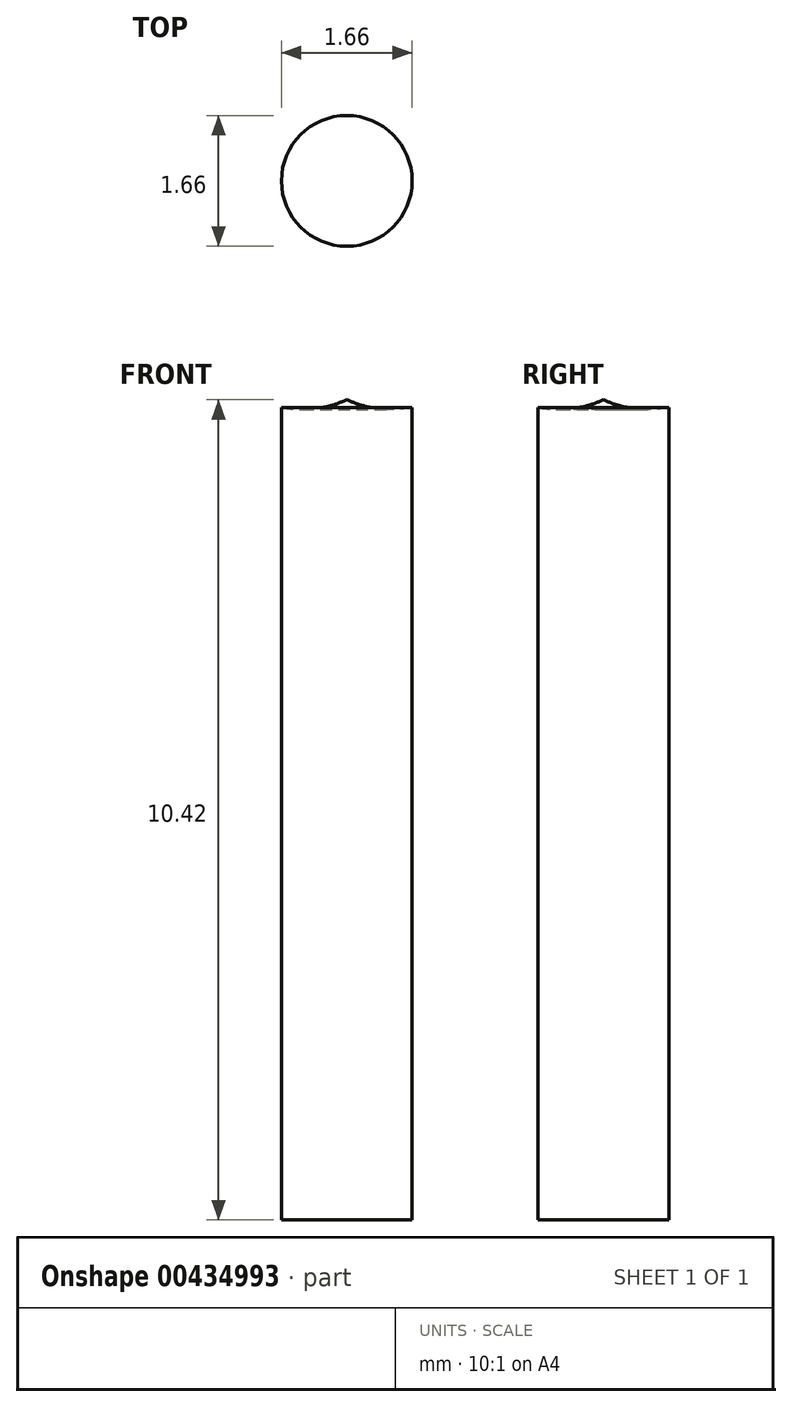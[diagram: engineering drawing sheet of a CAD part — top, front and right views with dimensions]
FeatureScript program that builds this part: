
annotation { "Feature Type Name" : "Feature", "Feature Type Description" : "" }
export const myFeature = defineFeature(function(context is Context, id is Id, definition is map)
    precondition{}
    {
        {
            var Q0;
            Q0=qCreatedBy(makeId("Front.planeOp"),FACE);
            var sketch = newSketch(context, id + "F0", { "sketchPlane" : qUnion([Q0])});
            skLineSegment(sketch, "E0", {"start": v(0, 0) * mm, "end": v(0, 2.45) * mm});
            skArc(sketch, "E1", {"start": v(0, 0) * mm, "mid": v(1.92, 1.22) * mm, "end": v(0, 2.45) * mm});
            skSolve(sketch);
        }
        {
            var Q0;
            Q0=makeQuery(id+"F0.imprint","IMPRINT",FACE,{"disambiguationData":[TD([[makeQuery(id+"F0.imprint","IMPRINT",EDGE,{"derivedFrom":sQuery(id+"F0.wireOp",EDGE,"E0")}),-1.0]])]});
            var Q1;
            Q1=sQuery(id+"F0.wireOp",EDGE,"E0");
            revolve(context, id + "F1", {"entities" : qUnion([Q0]), "axis" : qUnion([Q1]), "revolveType" : RevolveType.FULL});
        }
        {
            var Q0;
            Q0=qCreatedBy(makeId("Top.planeOp"),FACE);
            var sketch = newSketch(context, id + "F2", { "sketchPlane" : qUnion([Q0])});
            skCircle(sketch, "E2", {"center": v(0, 0) * mm, "radius": 0.83 * mm});
            skSolve(sketch);
        }
        {
            var Q0;
            Q0 = qSketchRegion(id + "F2", true);
            extrude(context, id + "F3", {"entities" : qUnion([Q0]), "operationType" : NewBodyOperationType.ADD, "oppositeDirection" : true, "depth" : 10.42 * mm});
        }
    });
